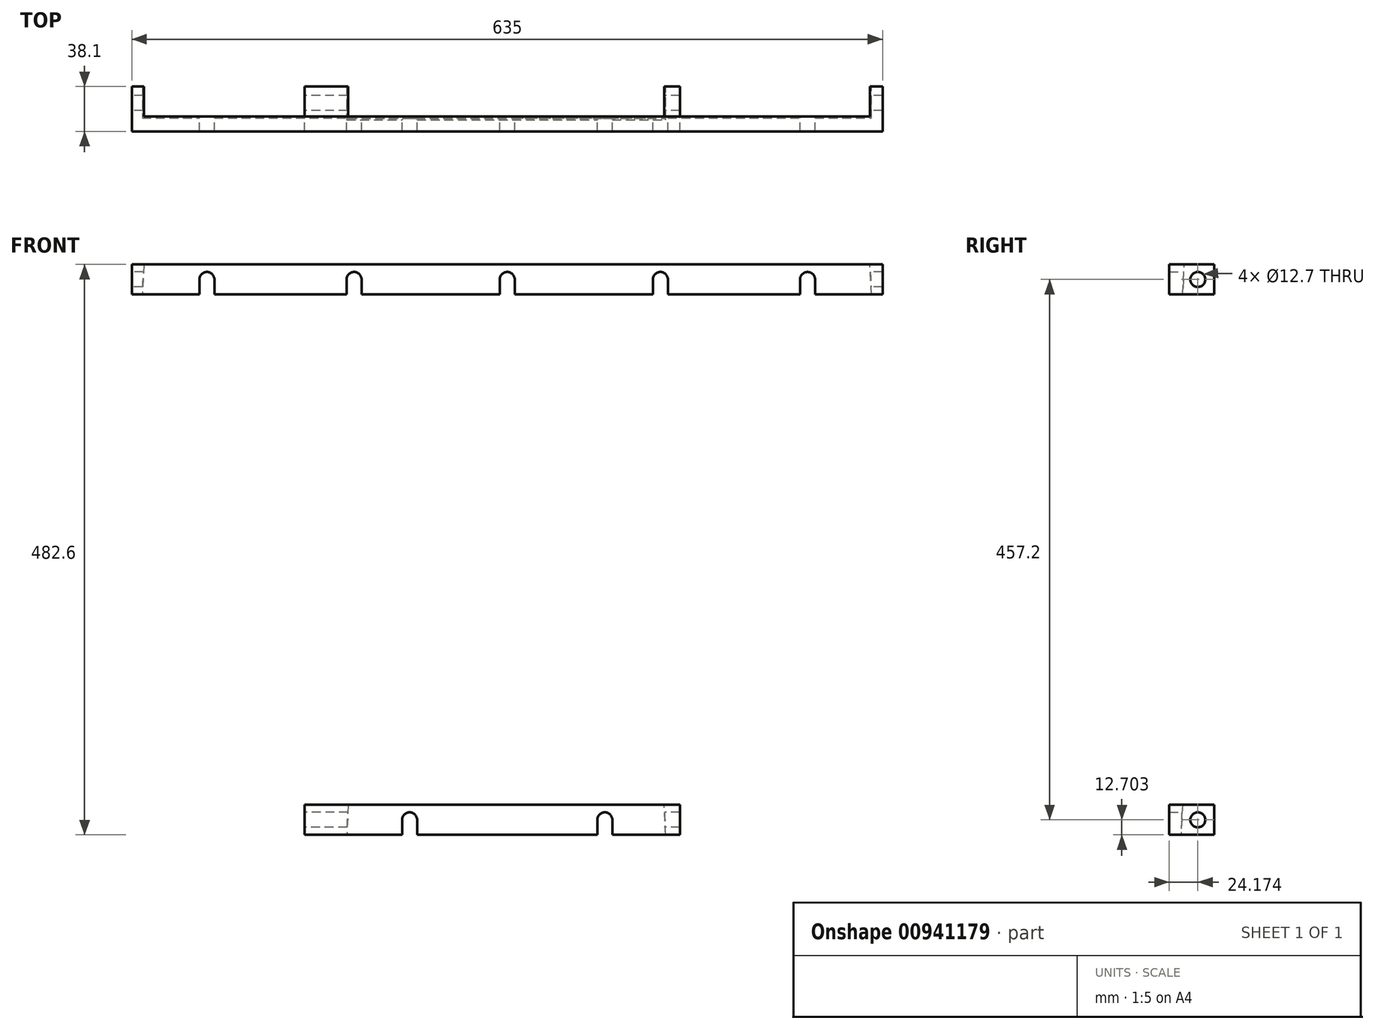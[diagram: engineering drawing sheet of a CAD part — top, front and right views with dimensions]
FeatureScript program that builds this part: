
annotation { "Feature Type Name" : "Feature", "Feature Type Description" : "" }
export const myFeature = defineFeature(function(context is Context, id is Id, definition is map)
    precondition{}
    {
        {
            var Q0;
            Q0=qCreatedBy(makeId("Front.planeOp"),FACE);
            var sketch = newSketch(context, id + "F0", { "sketchPlane" : qUnion([Q0])});
            skLineSegment(sketch, "E0", {"start": v(-360.77, 337.5) * mm, "end": v(-360.77, 95.66) * mm, "construction": true});
            skLineSegment(sketch, "E1", {"start": v(-411.57, 362.73) * mm, "end": v(-411.57, 83.04) * mm, "construction": true});
            skLineSegment(sketch, "E2", {"start": v(-236.3, 337.5) * mm, "end": v(-236.3, 91.45) * mm, "construction": true});
            skLineSegment(sketch, "E3", {"start": v(-106.77, 327.44) * mm, "end": v(-106.77, 58.26) * mm, "construction": true});
            skLineSegment(sketch, "E4", {"start": v(22.77, 348.47) * mm, "end": v(22.77, 1.48) * mm, "construction": true});
            skLineSegment(sketch, "E5", {"start": v(147.23, 394.87) * mm, "end": v(147.23, 20.26) * mm, "construction": true});
            skLineSegment(sketch, "E6", {"start": v(198.03, 457.82) * mm, "end": v(198.03, 75.08) * mm, "construction": true});
            skLineSegment(sketch, "E7", {"start": v(26.58, -116.2) * mm, "end": v(26.58, -360.14) * mm, "construction": true});
            skLineSegment(sketch, "E8", {"start": v(-240.12, -128.8) * mm, "end": v(-240.12, -419.02) * mm, "construction": true});
            skLineSegment(sketch, "E9", {"start": v(-189.32, -128.7) * mm, "end": v(-189.32, -411.1) * mm, "construction": true});
            skLineSegment(sketch, "E10", {"start": v(-24.22, -137.36) * mm, "end": v(-24.22, -379.95) * mm, "construction": true});
            skLineSegment(sketch, "E11", {"start": v(-495.14, 207.58) * mm, "end": v(380.47, 207.58) * mm, "construction": true});
            skLineSegment(sketch, "E12", {"start": v(-343.86, -249.62) * mm, "end": v(198.03, -249.62) * mm, "construction": true});
            skArc(sketch, "E13", {"start": v(-354.42, 207.58) * mm, "mid": v(-360.77, 213.93) * mm, "end": v(-367.12, 207.58) * mm});
            skArc(sketch, "E14", {"start": v(-229.96, 207.58) * mm, "mid": v(-236.3, 213.93) * mm, "end": v(-242.66, 207.58) * mm});
            skArc(sketch, "E15", {"start": v(-100.42, 207.58) * mm, "mid": v(-106.77, 213.93) * mm, "end": v(-113.12, 207.58) * mm});
            skArc(sketch, "E16", {"start": v(29.12, 207.58) * mm, "mid": v(22.77, 213.93) * mm, "end": v(16.42, 207.58) * mm});
            skArc(sketch, "E17", {"start": v(153.58, 207.55) * mm, "mid": v(147.23, 213.92) * mm, "end": v(140.88, 207.55) * mm});
            skArc(sketch, "E18", {"start": v(-182.97, -249.62) * mm, "mid": v(-189.32, -243.27) * mm, "end": v(-195.67, -249.62) * mm});
            skArc(sketch, "E19", {"start": v(-17.87, -249.62) * mm, "mid": v(-24.22, -243.27) * mm, "end": v(-30.57, -249.62) * mm});
            skLineSegment(sketch, "E20.bottom", {"start": v(-411.57, 220.28) * mm, "end": v(198.03, 220.28) * mm});
            skLineSegment(sketch, "E20.top", {"start": v(-411.57, 194.88) * mm, "end": v(198.03, 194.88) * mm});
            skLineSegment(sketch, "E20.right", {"start": v(198.03, 220.28) * mm, "end": v(198.03, 194.88) * mm});
            skLineSegment(sketch, "E21.bottom", {"start": v(-252.82, -236.92) * mm, "end": v(39.28, -236.92) * mm});
            skLineSegment(sketch, "E21.top", {"start": v(-252.82, -262.32) * mm, "end": v(39.28, -262.32) * mm});
            skLineSegment(sketch, "E21.left", {"start": v(-252.82, -236.92) * mm, "end": v(-252.82, -262.32) * mm});
            skLineSegment(sketch, "E21.right", {"start": v(39.28, -236.92) * mm, "end": v(39.28, -262.32) * mm});
            skLineSegment(sketch, "E22.bottom", {"start": v(-411.57, 220.28) * mm, "end": v(-424.27, 220.28) * mm});
            skLineSegment(sketch, "E22.top", {"start": v(-411.57, 194.88) * mm, "end": v(-424.27, 194.88) * mm});
            skLineSegment(sketch, "E22.right", {"start": v(-424.27, 220.28) * mm, "end": v(-424.27, 194.88) * mm});
            skLineSegment(sketch, "E23.bottom", {"start": v(198.03, 220.28) * mm, "end": v(210.73, 220.28) * mm});
            skLineSegment(sketch, "E23.top", {"start": v(198.03, 194.88) * mm, "end": v(210.73, 194.88) * mm});
            skLineSegment(sketch, "E23.right", {"start": v(210.73, 220.28) * mm, "end": v(210.73, 194.88) * mm});
            skLineSegment(sketch, "E24", {"start": v(-367.12, 207.58) * mm, "end": v(-367.12, 194.88) * mm});
            skLineSegment(sketch, "E25", {"start": v(-354.42, 207.58) * mm, "end": v(-354.42, 194.88) * mm});
            skLineSegment(sketch, "E26", {"start": v(-242.66, 207.58) * mm, "end": v(-242.66, 194.88) * mm});
            skLineSegment(sketch, "E27", {"start": v(-229.96, 207.58) * mm, "end": v(-229.96, 194.88) * mm});
            skLineSegment(sketch, "E28", {"start": v(-113.12, 207.58) * mm, "end": v(-113.12, 194.88) * mm});
            skLineSegment(sketch, "E29", {"start": v(-100.42, 207.58) * mm, "end": v(-100.42, 194.88) * mm});
            skLineSegment(sketch, "E30", {"start": v(16.42, 207.58) * mm, "end": v(16.42, 194.88) * mm});
            skLineSegment(sketch, "E31", {"start": v(29.12, 207.58) * mm, "end": v(29.12, 194.88) * mm});
            skLineSegment(sketch, "E32", {"start": v(140.88, 207.58) * mm, "end": v(140.88, 194.88) * mm});
            skLineSegment(sketch, "E33", {"start": v(153.58, 207.58) * mm, "end": v(153.58, 194.88) * mm});
            skLineSegment(sketch, "E34", {"start": v(-195.67, -249.62) * mm, "end": v(-195.67, -262.32) * mm});
            skPoint(sketch, "E34.endSnap0", {"position": v(-106.77, -262.32) * mm});
            skLineSegment(sketch, "E35", {"start": v(-182.97, -249.62) * mm, "end": v(-182.97, -262.32) * mm});
            skLineSegment(sketch, "E36", {"start": v(-30.57, -249.62) * mm, "end": v(-30.57, -262.32) * mm});
            skLineSegment(sketch, "E37", {"start": v(-17.87, -249.62) * mm, "end": v(-17.87, -262.32) * mm});
            skSolve(sketch);
        }
        {
            var Q0;
            Q0=makeQuery(id+"F0.imprint","IMPRINT",FACE,{"disambiguationData":[TD([[makeQuery(id+"F0.imprint","IMPRINT",EDGE,{"derivedFrom":sQuery(id+"F0.wireOp",EDGE,"E20.right")}),1.0]])]});
            var Q1;
            Q1=makeQuery(id+"F0.imprint","IMPRINT",FACE,{"disambiguationData":[TD([[makeQuery(id+"F0.imprint","IMPRINT",EDGE,{"derivedFrom":sQuery(id+"F0.wireOp",EDGE,"E18")}),-1.0]])]});
            var Q2;
            Q2=makeQuery(id+"F0.imprint","IMPRINT",FACE,{"disambiguationData":[TD([[makeQuery(id+"F0.imprint","IMPRINT",EDGE,{"derivedFrom":sQuery(id+"F0.wireOp",EDGE,"E13")}),-1.0]])]});
            extrude(context, id + "F1", {"entities" : qUnion([Q0, Q1, Q2]), "depth" : 38.1 * mm, "offsetDistance" : 25.4 * mm});
        }
        {
            var Q0;
            Q0=makeQuery(id+"F1.opExtrude","SWEPT_FACE",FACE,{"disambiguationData":[OSD([sQuery(id+"F0.wireOp",EDGE,"E20.bottom"),sQuery(id+"F0.wireOp",EDGE,"E22.bottom"),sQuery(id+"F0.wireOp",EDGE,"E23.bottom")])]});
            var sketch = newSketch(context, id + "F2", { "sketchPlane" : qUnion([Q0])});
            skLineSegment(sketch, "E38.bottom", {"start": v(-414.12, 0) * mm, "end": v(200.02, 0) * mm});
            skLineSegment(sketch, "E38.top", {"start": v(-414.12, -25.45) * mm, "end": v(200.02, -25.45) * mm});
            skLineSegment(sketch, "E38.left", {"start": v(-414.12, 0) * mm, "end": v(-414.12, -25.45) * mm});
            skLineSegment(sketch, "E38.right", {"start": v(200.02, 0) * mm, "end": v(200.02, -25.45) * mm});
            skSolve(sketch);
        }
        {
            var Q0;
            Q0=makeQuery(id+"F2.imprint","IMPRINT",FACE,{"disambiguationData":[TD([[makeQuery(id+"F2.imprint","IMPRINT",EDGE,{"derivedFrom":sQuery(id+"F2.wireOp",EDGE,"E38.bottom")}),-1.0]])]});
            extrude(context, id + "F3", {"entities" : qUnion([Q0]), "operationType" : NewBodyOperationType.REMOVE, "oppositeDirection" : true, "depth" : 25.4 * mm, "offsetDistance" : 25.4 * mm, "hasDraft" : true, "draftAngle" : 3 * degree});
        }
        {
            var Q0;
            Q0=makeQuery(id+"F1.opExtrude","SWEPT_FACE",FACE,{"disambiguationData":[OSD([sQuery(id+"F0.wireOp",EDGE,"E21.bottom")])]});
            var sketch = newSketch(context, id + "F4", { "sketchPlane" : qUnion([Q0])});
            skLineSegment(sketch, "E39.bottom", {"start": v(25.84, 0) * mm, "end": v(-241.2, 0) * mm});
            skLineSegment(sketch, "E39.top", {"start": v(25.84, -26.89) * mm, "end": v(-241.2, -26.89) * mm});
            skLineSegment(sketch, "E39.left", {"start": v(25.84, 0) * mm, "end": v(25.84, -26.89) * mm});
            skLineSegment(sketch, "E39.right", {"start": v(-241.2, 0) * mm, "end": v(-241.2, -26.89) * mm});
            skSolve(sketch);
        }
        {
            var Q0;
            Q0 = qSketchRegion(id + "F4", true);
            extrude(context, id + "F5", {"entities" : qUnion([Q0]), "operationType" : NewBodyOperationType.REMOVE, "oppositeDirection" : true, "depth" : 25.4 * mm, "offsetDistance" : 25.4 * mm, "hasDraft" : true, "draftAngle" : 3 * degree});
        }
        {
            var Q0;
            Q0=makeQuery(id+"F1.opExtrude","SWEPT_FACE",FACE,{"disambiguationData":[OSD([sQuery(id+"F0.wireOp",EDGE,"E21.left")])]});
            extrude(context, id + "F6", {"entities" : qUnion([Q0]), "operationType" : NewBodyOperationType.ADD, "depth" : 25.4 * mm, "offsetDistance" : 25.4 * mm});
        }
        {
            var Q0;
            Q0=qCreatedBy(makeId("Right.planeOp"),FACE);
            var sketch = newSketch(context, id + "F7", { "sketchPlane" : qUnion([Q0])});
            skLineSegment(sketch, "E40", {"start": v(-13.93, 275.26) * mm, "end": v(-13.93, -305.9) * mm, "construction": true});
            skLineSegment(sketch, "E41", {"start": v(0, 207.58) * mm, "end": v(-96.74, 207.58) * mm, "construction": true});
            skLineSegment(sketch, "E42", {"start": v(0, -249.62) * mm, "end": v(-76.26, -249.62) * mm, "construction": true});
            skCircle(sketch, "E43", {"center": v(-13.93, 207.58) * mm, "radius": 6.35 * mm});
            skCircle(sketch, "E44", {"center": v(-13.93, -249.62) * mm, "radius": 6.35 * mm});
            skSolve(sketch);
        }
        {
            var Q0;
            Q0 = qSketchRegion(id + "F7", true);
            extrude(context, id + "F8", {"entities" : qUnion([Q0]), "operationType" : NewBodyOperationType.REMOVE, "depth" : 508 * mm, "offsetDistance" : 25.4 * mm, "hasSecondDirection" : true, "secondDirectionOppositeDirection" : true, "secondDirectionDepth" : 508 * mm});
        }
    });
